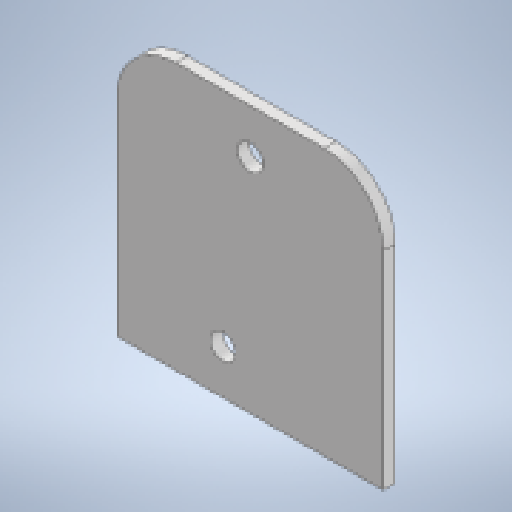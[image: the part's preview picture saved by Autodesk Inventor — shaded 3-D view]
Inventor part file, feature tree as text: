
AUTODESK INVENTOR PART (.ipt)
format: ipt  version: 2025 (Build 290162010, 162A)  size: 146,432 bytes
history: native  units: mm
features: sketch x2, sheet_metal_op x1, hole x1, fillet x1, other x1
ambient origin geometry x8: Origin, YZ Plane, XZ Plane, XY Plane, X Axis, Y Axis, Z Axis, Center Point
bodies: Solid1 (feature_tree)
feature tree (6):
  sheet_metal_op  "Face1"
  hole  "Hole1"  [1 undecoded]
  fillet  "Fillet1"  Radius=8.0mm
  sketch  "Sketch1"  dims[d0=180.0mm d1=180.0mm d2=8.0mm]
  other  "Plate1"
  sketch  "Sketch2"  dims[d3=17.0mm d4=6.0mm d5=4.0mm d6=2.0mm d7=90.0deg d8=8.0mm d9=20.594885mm d15=60.0mm d16=40.0mm]
note: 1 required parameter value undecoded (feature->parameter linkage not recoverable at this tier; creation-order binding heuristic only, values carry confidence <= 0.55)
